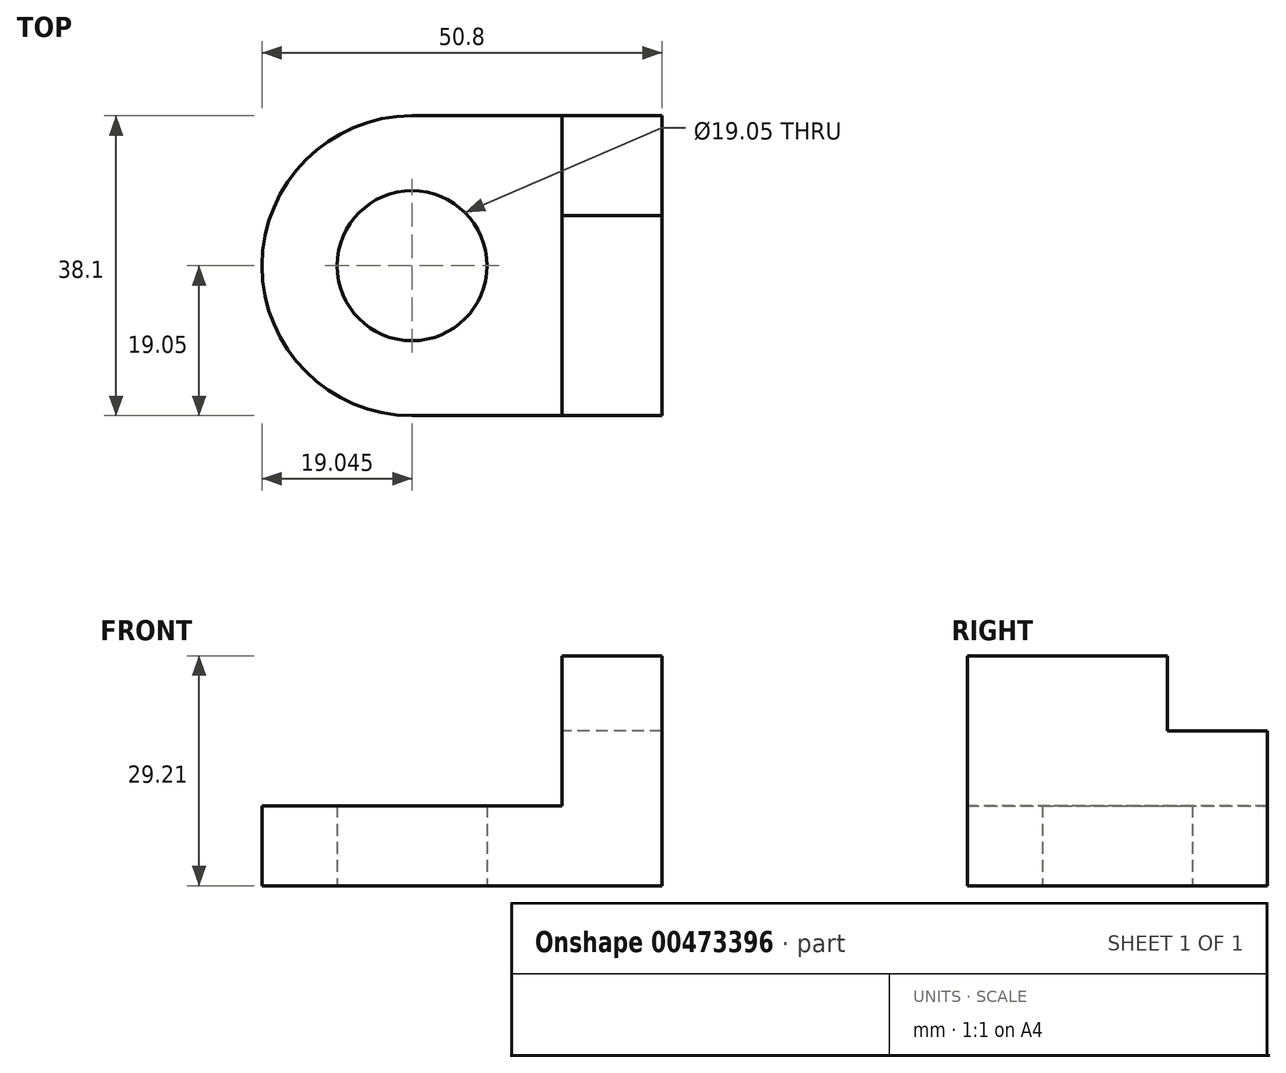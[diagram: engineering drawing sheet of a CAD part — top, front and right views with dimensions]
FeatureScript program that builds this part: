
annotation { "Feature Type Name" : "Feature", "Feature Type Description" : "" }
export const myFeature = defineFeature(function(context is Context, id is Id, definition is map)
    precondition{}
    {
        {
            var Q0;
            Q0=qCreatedBy(makeId("Top.planeOp"),FACE);
            var sketch = newSketch(context, id + "F0", { "sketchPlane" : qUnion([Q0])});
            skLineSegment(sketch, "E0.bottom", {"start": v(15.88, 19.05) * mm, "end": v(-15.88, 19.05) * mm});
            skLineSegment(sketch, "E0.top", {"start": v(15.88, -19.05) * mm, "end": v(-15.88, -19.05) * mm});
            skLineSegment(sketch, "E0.left", {"start": v(15.88, 19.05) * mm, "end": v(15.88, -19.05) * mm});
            skLineSegment(sketch, "E0.right", {"start": v(-15.88, 19.05) * mm, "end": v(-15.88, -19.05) * mm});
            skPoint(sketch, "E0.middle", {"position": v(0, 0) * mm});
            skCircle(sketch, "E1", {"center": v(-15.88, 0) * mm, "radius": 19.05 * mm});
            skCircle(sketch, "E2", {"center": v(-15.88, 0) * mm, "radius": 9.53 * mm});
            skSolve(sketch);
        }
        {
            var Q0;
            Q0 = qSketchRegion(id + "F0", true);
            extrude(context, id + "F1", {"entities" : qUnion([Q0]), "depth" : 10.16 * mm});
        }
        {
            var Q0;
            Q0=makeQuery(id+"F1.opExtrude","CAP_FACE",FACE,{"disambiguationData":[OSD([sQuery(id+"F0.wireOp",EDGE,"E0.bottom"),sQuery(id+"F0.wireOp",EDGE,"E0.top"),sQuery(id+"F0.wireOp",EDGE,"E0.left"),sQuery(id+"F0.wireOp",EDGE,"E1"),sQuery(id+"F0.wireOp",EDGE,"E2")])],"isStart":false});
            var sketch = newSketch(context, id + "F2", { "sketchPlane" : qUnion([Q0])});
            skLineSegment(sketch, "E3.bottom", {"start": v(15.88, -19.05) * mm, "end": v(3.17, -19.05) * mm});
            skLineSegment(sketch, "E3.top", {"start": v(15.88, 6.35) * mm, "end": v(3.17, 6.35) * mm});
            skLineSegment(sketch, "E3.left", {"start": v(15.88, -19.05) * mm, "end": v(15.88, 6.35) * mm});
            skLineSegment(sketch, "E3.right", {"start": v(3.17, -19.05) * mm, "end": v(3.17, 6.35) * mm});
            skSolve(sketch);
        }
        {
            var Q0;
            Q0=makeQuery(id+"F2.imprint","IMPRINT",FACE,{"disambiguationData":[TD([[makeQuery(id+"F2.imprint","IMPRINT",EDGE,{"derivedFrom":sQuery(id+"F2.wireOp",EDGE,"E3.bottom")}),-1.0]])]});
            extrude(context, id + "F3", {"entities" : qUnion([Q0]), "operationType" : NewBodyOperationType.ADD, "depth" : 15.24 * mm});
        }
        {
            var Q0;
            Q0=makeQuery(id+"F1.opExtrude","CAP_FACE",FACE,{"disambiguationData":[OSD([sQuery(id+"F0.wireOp",EDGE,"E0.bottom"),sQuery(id+"F0.wireOp",EDGE,"E0.top"),sQuery(id+"F0.wireOp",EDGE,"E0.left"),sQuery(id+"F0.wireOp",EDGE,"E1"),sQuery(id+"F0.wireOp",EDGE,"E2")])],"isStart":false});
            var sketch = newSketch(context, id + "F4", { "sketchPlane" : qUnion([Q0])});
            skLineSegment(sketch, "E4.bottom", {"start": v(15.88, 6.35) * mm, "end": v(3.17, 6.35) * mm});
            skLineSegment(sketch, "E4.top", {"start": v(15.88, 19.05) * mm, "end": v(3.17, 19.05) * mm});
            skLineSegment(sketch, "E4.left", {"start": v(15.88, 6.35) * mm, "end": v(15.88, 19.05) * mm});
            skLineSegment(sketch, "E4.right", {"start": v(3.17, 6.35) * mm, "end": v(3.17, 19.05) * mm});
            skSolve(sketch);
        }
        {
            var Q0;
            Q0=makeQuery(id+"F4.imprint","IMPRINT",FACE,{"disambiguationData":[TD([[makeQuery(id+"F4.imprint","IMPRINT",EDGE,{"derivedFrom":sQuery(id+"F4.wireOp",EDGE,"E4.bottom")}),-1.0]])]});
            extrude(context, id + "F5", {"entities" : qUnion([Q0]), "operationType" : NewBodyOperationType.ADD, "depth" : 9.52 * mm});
        }
        {
            var Q0;
            Q0=makeQuery(id+"F3.opExtrude","CAP_FACE",FACE,{"disambiguationData":[OSD([sQuery(id+"F2.wireOp",EDGE,"E3.bottom"),sQuery(id+"F2.wireOp",EDGE,"E3.top"),sQuery(id+"F2.wireOp",EDGE,"E3.left"),sQuery(id+"F2.wireOp",EDGE,"E3.right")])],"isStart":false});
            extrude(context, id + "F6", {"entities" : qUnion([Q0]), "operationType" : NewBodyOperationType.ADD, "depth" : 3.8 * mm});
        }
    });
